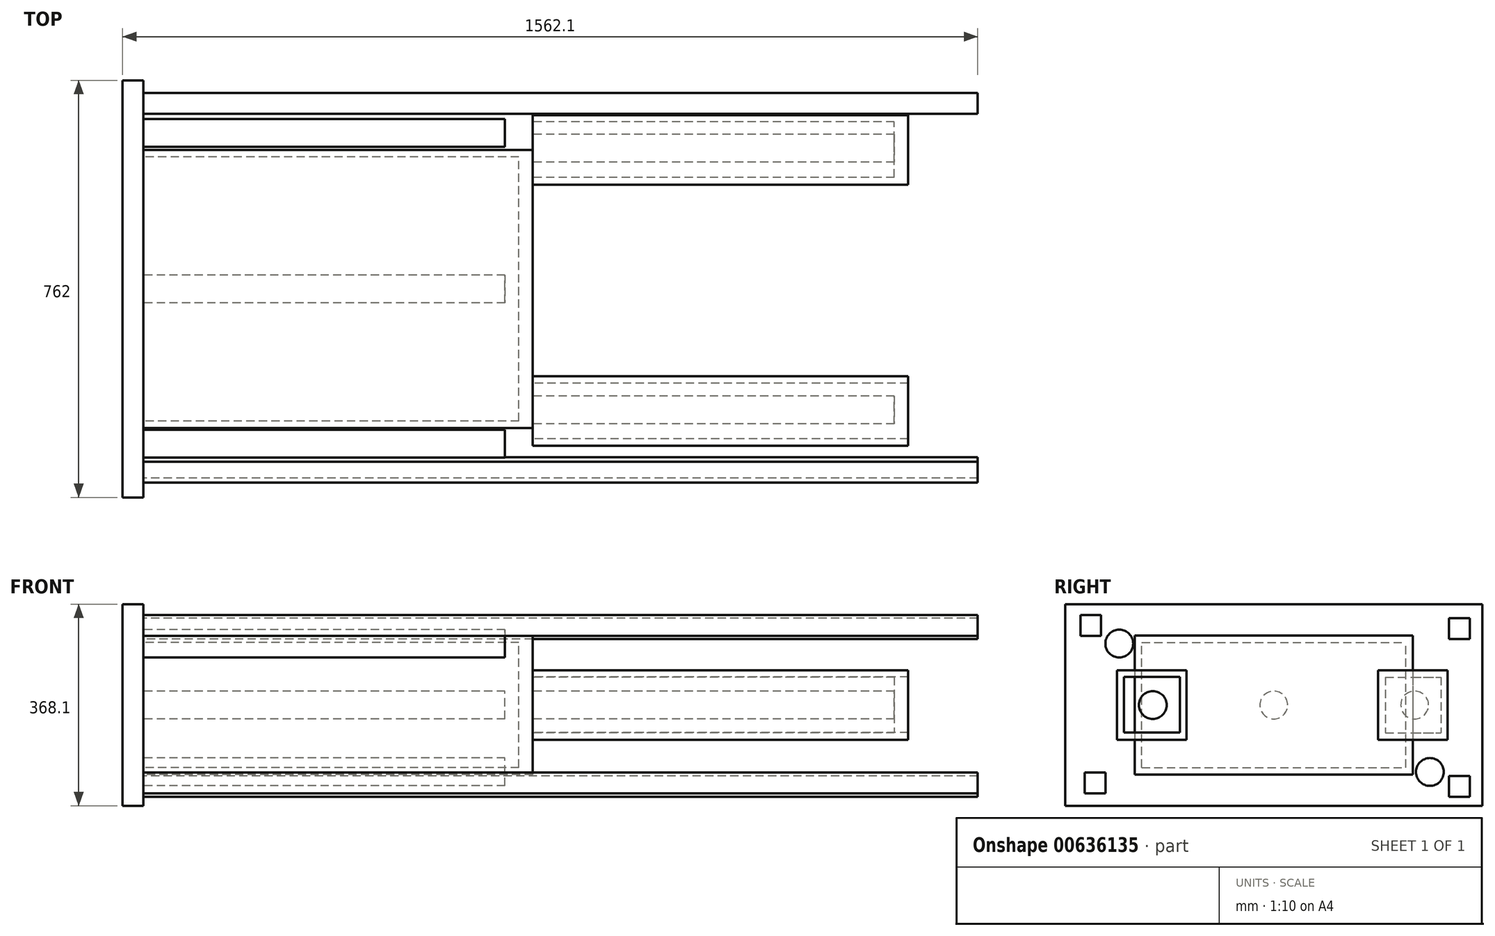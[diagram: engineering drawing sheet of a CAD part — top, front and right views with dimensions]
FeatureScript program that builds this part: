
annotation { "Feature Type Name" : "Feature", "Feature Type Description" : "" }
export const myFeature = defineFeature(function(context is Context, id is Id, definition is map)
    precondition{}
    {
        {
            var Q0;
            Q0=qCreatedBy(makeId("Right.planeOp"),FACE);
            var sketch = newSketch(context, id + "F0", { "sketchPlane" : qUnion([Q0])});
            skLineSegment(sketch, "E0.bottom", {"start": v(254, 127) * mm, "end": v(-254, 127) * mm});
            skLineSegment(sketch, "E0.top", {"start": v(254, -127) * mm, "end": v(-254, -127) * mm});
            skLineSegment(sketch, "E0.left", {"start": v(254, 127) * mm, "end": v(254, -127) * mm});
            skLineSegment(sketch, "E0.right", {"start": v(-254, 127) * mm, "end": v(-254, -127) * mm});
            skPoint(sketch, "E0.middle", {"position": v(0, 0) * mm});
            skSolve(sketch);
        }
        {
            var Q0;
            Q0 = qSketchRegion(id + "F0", true);
            extrude(context, id + "F1", {"entities" : qUnion([Q0]), "depth" : 711.2 * mm, "offsetDistance" : 25.4 * mm});
        }
        {
            var Q0;
            Q0=makeQuery(id+"F1.opExtrude","CAP_FACE",FACE,{"disambiguationData":[OSD([sQuery(id+"F0.wireOp",EDGE,"E0.bottom"),sQuery(id+"F0.wireOp",EDGE,"E0.top"),sQuery(id+"F0.wireOp",EDGE,"E0.left"),sQuery(id+"F0.wireOp",EDGE,"E0.right")])],"isStart":true});
            var sketch = newSketch(context, id + "F2", { "sketchPlane" : qUnion([Q0])});
            skLineSegment(sketch, "E1.bottom", {"start": v(241.3, -114.3) * mm, "end": v(-241.3, -114.3) * mm});
            skLineSegment(sketch, "E1.top", {"start": v(241.3, 114.3) * mm, "end": v(-241.3, 114.3) * mm});
            skLineSegment(sketch, "E1.left", {"start": v(241.3, -114.3) * mm, "end": v(241.3, 114.3) * mm});
            skLineSegment(sketch, "E1.right", {"start": v(-241.3, -114.3) * mm, "end": v(-241.3, 114.3) * mm});
            skPoint(sketch, "E1.middle", {"position": v(0, 0) * mm});
            skSolve(sketch);
        }
        {
            var Q0;
            Q0=makeQuery(id+"F2.imprint","IMPRINT",FACE,{"disambiguationData":[TD([[makeQuery(id+"F2.imprint","IMPRINT",EDGE,{"derivedFrom":sQuery(id+"F2.wireOp",EDGE,"E1.bottom")}),-1.0]])]});
            extrude(context, id + "F3", {"entities" : qUnion([Q0]), "operationType" : NewBodyOperationType.REMOVE, "oppositeDirection" : true, "depth" : 685.8 * mm, "offsetDistance" : 25.4 * mm});
        }
        {
            var Q0;
            Q0=qCreatedBy(makeId("Right.planeOp"),FACE);
            var sketch = newSketch(context, id + "F4", { "sketchPlane" : qUnion([Q0])});
            skCircle(sketch, "E2", {"center": v(0, 0) * mm, "radius": 25.4 * mm});
            skSolve(sketch);
        }
        {
            var Q0;
            Q0=makeQuery(id+"F4.imprint","IMPRINT",FACE,{"disambiguationData":[TD([[makeQuery(id+"F4.imprint","IMPRINT",EDGE,{"derivedFrom":sQuery(id+"F4.wireOp",EDGE,"E2")}),1.0]])]});
            extrude(context, id + "F5", {"entities" : qUnion([Q0]), "depth" : 660.4 * mm, "offsetDistance" : 25.4 * mm});
        }
        {
            var Q0;
            Q0=makeQuery(id+"F1.opExtrude","CAP_FACE",FACE,{"disambiguationData":[OSD([sQuery(id+"F0.wireOp",EDGE,"E0.bottom"),sQuery(id+"F0.wireOp",EDGE,"E0.top"),sQuery(id+"F0.wireOp",EDGE,"E0.left"),sQuery(id+"F0.wireOp",EDGE,"E0.right")])],"isStart":false});
            var sketch = newSketch(context, id + "F6", { "sketchPlane" : qUnion([Q0])});
            skLineSegment(sketch, "E3.bottom", {"start": v(-286.75, 63.5) * mm, "end": v(-159.75, 63.5) * mm});
            skLineSegment(sketch, "E3.top", {"start": v(-286.75, -63.5) * mm, "end": v(-159.75, -63.5) * mm});
            skLineSegment(sketch, "E3.left", {"start": v(-286.75, 63.5) * mm, "end": v(-286.75, -63.5) * mm});
            skLineSegment(sketch, "E3.right", {"start": v(-159.75, 63.5) * mm, "end": v(-159.75, -63.5) * mm});
            skPoint(sketch, "E3.middle", {"position": v(-223.25, 0) * mm});
            skSolve(sketch);
        }
        {
            var Q0;
            Q0=makeQuery(id+"F6.imprint","IMPRINT",FACE,{"disambiguationData":[TD([[makeQuery(id+"F6.imprint","IMPRINT",EDGE,{"derivedFrom":sQuery(id+"F6.wireOp",EDGE,"E3.bottom")}),-1.0]])]});
            extrude(context, id + "F7", {"entities" : qUnion([Q0]), "operationType" : NewBodyOperationType.ADD, "depth" : 685.8 * mm, "offsetDistance" : 25.4 * mm});
        }
        {
            var Q0;
            Q0=makeQuery(id+"F1.opExtrude","CAP_FACE",FACE,{"disambiguationData":[OSD([sQuery(id+"F0.wireOp",EDGE,"E0.bottom"),sQuery(id+"F0.wireOp",EDGE,"E0.top"),sQuery(id+"F0.wireOp",EDGE,"E0.left"),sQuery(id+"F0.wireOp",EDGE,"E0.right")])],"isStart":false});
            var sketch = newSketch(context, id + "F8", { "sketchPlane" : qUnion([Q0])});
            skLineSegment(sketch, "E4.bottom", {"start": v(-171.9, -50.19) * mm, "end": v(-273.5, -50.19) * mm});
            skLineSegment(sketch, "E4.top", {"start": v(-171.9, 51.41) * mm, "end": v(-273.5, 51.41) * mm});
            skLineSegment(sketch, "E4.left", {"start": v(-171.9, -50.19) * mm, "end": v(-171.9, 51.41) * mm});
            skLineSegment(sketch, "E4.right", {"start": v(-273.5, -50.19) * mm, "end": v(-273.5, 51.41) * mm});
            skSolve(sketch);
        }
        {
            var Q0;
            Q0=makeQuery(id+"F8.imprint","IMPRINT",FACE,{"disambiguationData":[TD([[makeQuery(id+"F8.imprint","IMPRINT",EDGE,{"derivedFrom":sQuery(id+"F8.wireOp",EDGE,"E4.bottom")}),-1.0]])]});
            extrude(context, id + "F9", {"entities" : qUnion([Q0]), "operationType" : NewBodyOperationType.REMOVE, "depth" : 685.8 * mm, "offsetDistance" : 25.4 * mm});
        }
        {
            var Q0;
            Q0=makeQuery(id+"F1.opExtrude","CAP_FACE",FACE,{"disambiguationData":[OSD([sQuery(id+"F0.wireOp",EDGE,"E0.bottom"),sQuery(id+"F0.wireOp",EDGE,"E0.top"),sQuery(id+"F0.wireOp",EDGE,"E0.left"),sQuery(id+"F0.wireOp",EDGE,"E0.right")])],"isStart":false});
            var sketch = newSketch(context, id + "F10", { "sketchPlane" : qUnion([Q0])});
            skCircle(sketch, "E5", {"center": v(-221.22, 0) * mm, "radius": 25.4 * mm});
            skSolve(sketch);
        }
        {
            var Q0;
            Q0=makeQuery(id+"F10.imprint","IMPRINT",FACE,{"disambiguationData":[TD([[makeQuery(id+"F10.imprint","IMPRINT",EDGE,{"derivedFrom":sQuery(id+"F10.wireOp",EDGE,"E5")}),1.0]])]});
            extrude(context, id + "F11", {"entities" : qUnion([Q0]), "operationType" : NewBodyOperationType.ADD, "depth" : 660.4 * mm, "offsetDistance" : 25.4 * mm});
        }
        {
            var Q0;
            Q0=qCreatedBy(makeId("Right.planeOp"),FACE);
            var sketch = newSketch(context, id + "F12", { "sketchPlane" : qUnion([Q0])});
            skLineSegment(sketch, "E6.bottom", {"start": v(-381, 184.05) * mm, "end": v(381, 184.05) * mm});
            skLineSegment(sketch, "E6.top", {"start": v(-381, -184.05) * mm, "end": v(381, -184.05) * mm});
            skLineSegment(sketch, "E6.left", {"start": v(-381, 184.05) * mm, "end": v(-381, -184.05) * mm});
            skLineSegment(sketch, "E6.right", {"start": v(381, 184.05) * mm, "end": v(381, -184.05) * mm});
            skPoint(sketch, "E6.middle", {"position": v(0, 0) * mm});
            skSolve(sketch);
        }
        {
            var Q0;
            Q0=makeQuery(id+"F12.imprint","IMPRINT",FACE,{"disambiguationData":[TD([[makeQuery(id+"F12.imprint","IMPRINT",EDGE,{"derivedFrom":sQuery(id+"F12.wireOp",EDGE,"E6.bottom")}),-1.0]])]});
            extrude(context, id + "F13", {"entities" : qUnion([Q0]), "oppositeDirection" : true, "depth" : 38.1 * mm, "offsetDistance" : 25.4 * mm});
        }
        {
            var Q0;
            Q0=makeQuery(id+"F1.opExtrude","CAP_FACE",FACE,{"disambiguationData":[OSD([sQuery(id+"F0.wireOp",EDGE,"E0.bottom"),sQuery(id+"F0.wireOp",EDGE,"E0.top"),sQuery(id+"F0.wireOp",EDGE,"E0.left"),sQuery(id+"F0.wireOp",EDGE,"E0.right")])],"isStart":false});
            var sketch = newSketch(context, id + "F14", { "sketchPlane" : qUnion([Q0])});
            skLineSegment(sketch, "E7.bottom", {"start": v(317.5, 63.5) * mm, "end": v(190.5, 63.5) * mm});
            skLineSegment(sketch, "E7.top", {"start": v(317.5, -63.5) * mm, "end": v(190.5, -63.5) * mm});
            skLineSegment(sketch, "E7.left", {"start": v(317.5, 63.5) * mm, "end": v(317.5, -63.5) * mm});
            skLineSegment(sketch, "E7.right", {"start": v(190.5, 63.5) * mm, "end": v(190.5, -63.5) * mm});
            skPoint(sketch, "E7.middle", {"position": v(254, 0) * mm});
            skSolve(sketch);
        }
        {
            var Q0;
            {var subQ0=sQuery(id+"F14.wireOp",EDGE,"E7.right");Q0=makeQuery(id+"F14.imprint","IMPRINT",FACE,{"disambiguationData":[TD([[makeQuery(id+"F14.imprint","IMPRINT",EDGE,{"derivedFrom":subQ0}),1.0]])]});}
            var Q1;
            {var subQ0=sQuery(id+"F14.wireOp",EDGE,"E7.left");Q1=makeQuery(id+"F14.imprint","IMPRINT",FACE,{"disambiguationData":[TD([[makeQuery(id+"F14.imprint","IMPRINT",EDGE,{"derivedFrom":subQ0}),-1.0]])]});}
            extrude(context, id + "F15", {"entities" : qUnion([Q0, Q1]), "operationType" : NewBodyOperationType.ADD, "depth" : 685.8 * mm, "offsetDistance" : 25.4 * mm});
        }
        {
            var Q0;
            Q0=makeQuery(id+"F1.opExtrude","CAP_FACE",FACE,{"disambiguationData":[OSD([sQuery(id+"F0.wireOp",EDGE,"E0.bottom"),sQuery(id+"F0.wireOp",EDGE,"E0.top"),sQuery(id+"F0.wireOp",EDGE,"E0.left"),sQuery(id+"F0.wireOp",EDGE,"E0.right")])],"isStart":false});
            var sketch = newSketch(context, id + "F16", { "sketchPlane" : qUnion([Q0])});
            skLineSegment(sketch, "E8.bottom", {"start": v(203.8, 50.8) * mm, "end": v(305.4, 50.8) * mm});
            skLineSegment(sketch, "E8.top", {"start": v(203.8, -50.8) * mm, "end": v(305.4, -50.8) * mm});
            skLineSegment(sketch, "E8.left", {"start": v(203.8, 50.8) * mm, "end": v(203.8, -50.8) * mm});
            skLineSegment(sketch, "E8.right", {"start": v(305.4, 50.8) * mm, "end": v(305.4, -50.8) * mm});
            skPoint(sketch, "E8.middle", {"position": v(254.6, 0) * mm});
            skSolve(sketch);
        }
        {
            var Q0;
            Q0=makeQuery(id+"F16.imprint","IMPRINT",FACE,{"disambiguationData":[TD([[makeQuery(id+"F16.imprint","IMPRINT",EDGE,{"derivedFrom":sQuery(id+"F16.wireOp",EDGE,"E8.bottom")}),-1.0]])]});
            extrude(context, id + "F17", {"entities" : qUnion([Q0]), "operationType" : NewBodyOperationType.REMOVE, "depth" : 660.4 * mm, "offsetDistance" : 25.4 * mm});
        }
        {
            var Q0;
            Q0=makeQuery(id+"F1.opExtrude","CAP_FACE",FACE,{"disambiguationData":[OSD([sQuery(id+"F0.wireOp",EDGE,"E0.bottom"),sQuery(id+"F0.wireOp",EDGE,"E0.top"),sQuery(id+"F0.wireOp",EDGE,"E0.left"),sQuery(id+"F0.wireOp",EDGE,"E0.right")])],"isStart":false});
            var sketch = newSketch(context, id + "F18", { "sketchPlane" : qUnion([Q0])});
            skCircle(sketch, "E9", {"center": v(257.24, 0) * mm, "radius": 25.4 * mm});
            skSolve(sketch);
        }
        {
            var Q0;
            Q0=makeQuery(id+"F18.imprint","IMPRINT",FACE,{"disambiguationData":[TD([[makeQuery(id+"F18.imprint","IMPRINT",EDGE,{"derivedFrom":sQuery(id+"F18.wireOp",EDGE,"E9")}),1.0]])]});
            extrude(context, id + "F19", {"entities" : qUnion([Q0]), "depth" : 660.4 * mm, "offsetDistance" : 25.4 * mm});
        }
        {
            var Q0;
            Q0=makeQuery(id+"F13.opExtrude","CAP_FACE",FACE,{"disambiguationData":[OSD([sQuery(id+"F12.wireOp",EDGE,"E6.bottom"),sQuery(id+"F12.wireOp",EDGE,"E6.top"),sQuery(id+"F12.wireOp",EDGE,"E6.left"),sQuery(id+"F12.wireOp",EDGE,"E6.right")])],"isStart":true});
            var sketch = newSketch(context, id + "F20", { "sketchPlane" : qUnion([Q0])});
            skLineSegment(sketch, "E10.bottom", {"start": v(-353.51, 164.15) * mm, "end": v(-315.41, 164.15) * mm});
            skLineSegment(sketch, "E10.top", {"start": v(-353.51, 126.05) * mm, "end": v(-315.41, 126.05) * mm});
            skLineSegment(sketch, "E10.left", {"start": v(-353.51, 164.15) * mm, "end": v(-353.51, 126.05) * mm});
            skLineSegment(sketch, "E10.right", {"start": v(-315.41, 164.15) * mm, "end": v(-315.41, 126.05) * mm});
            skPoint(sketch, "E10.middle", {"position": v(-334.46, 145.1) * mm});
            skLineSegment(sketch, "E11.bottom", {"start": v(-307.52, -123.32) * mm, "end": v(-345.62, -123.32) * mm});
            skLineSegment(sketch, "E11.top", {"start": v(-307.52, -161.42) * mm, "end": v(-345.62, -161.42) * mm});
            skLineSegment(sketch, "E11.left", {"start": v(-307.52, -123.32) * mm, "end": v(-307.52, -161.42) * mm});
            skLineSegment(sketch, "E11.right", {"start": v(-345.62, -123.32) * mm, "end": v(-345.62, -161.42) * mm});
            skPoint(sketch, "E11.middle", {"position": v(-326.57, -142.37) * mm});
            skLineSegment(sketch, "E12.bottom", {"start": v(357.93, 158.52) * mm, "end": v(319.83, 158.52) * mm});
            skLineSegment(sketch, "E12.top", {"start": v(357.93, 120.42) * mm, "end": v(319.83, 120.42) * mm});
            skLineSegment(sketch, "E12.left", {"start": v(357.93, 158.52) * mm, "end": v(357.93, 120.42) * mm});
            skLineSegment(sketch, "E12.right", {"start": v(319.83, 158.52) * mm, "end": v(319.83, 120.42) * mm});
            skPoint(sketch, "E12.middle", {"position": v(338.88, 139.47) * mm});
            skLineSegment(sketch, "E13.bottom", {"start": v(320.2, -129.37) * mm, "end": v(358.3, -129.37) * mm});
            skLineSegment(sketch, "E13.top", {"start": v(320.2, -167.47) * mm, "end": v(358.3, -167.47) * mm});
            skLineSegment(sketch, "E13.left", {"start": v(320.2, -129.37) * mm, "end": v(320.2, -167.47) * mm});
            skLineSegment(sketch, "E13.right", {"start": v(358.3, -129.37) * mm, "end": v(358.3, -167.47) * mm});
            skPoint(sketch, "E13.middle", {"position": v(339.24, -148.42) * mm});
            skSolve(sketch);
        }
        {
            var Q0;
            Q0=makeQuery(id+"F20.imprint","IMPRINT",FACE,{"disambiguationData":[TD([[makeQuery(id+"F20.imprint","IMPRINT",EDGE,{"derivedFrom":sQuery(id+"F20.wireOp",EDGE,"E13.bottom")}),-1.0]])]});
            var Q1;
            Q1=makeQuery(id+"F20.imprint","IMPRINT",FACE,{"disambiguationData":[TD([[makeQuery(id+"F20.imprint","IMPRINT",EDGE,{"derivedFrom":sQuery(id+"F20.wireOp",EDGE,"E12.bottom")}),1.0]])]});
            var Q2;
            Q2=makeQuery(id+"F20.imprint","IMPRINT",FACE,{"disambiguationData":[TD([[makeQuery(id+"F20.imprint","IMPRINT",EDGE,{"derivedFrom":sQuery(id+"F20.wireOp",EDGE,"E10.bottom")}),-1.0]])]});
            var Q3;
            Q3=makeQuery(id+"F20.imprint","IMPRINT",FACE,{"disambiguationData":[TD([[makeQuery(id+"F20.imprint","IMPRINT",EDGE,{"derivedFrom":sQuery(id+"F20.wireOp",EDGE,"E11.bottom")}),1.0]])]});
            extrude(context, id + "F21", {"entities" : qUnion([Q0, Q1, Q2, Q3]), "operationType" : NewBodyOperationType.ADD, "depth" : 1524 * mm, "offsetDistance" : 25.4 * mm});
        }
        {
            var Q0;
            Q0=makeQuery(id+"F13.opExtrude","CAP_FACE",FACE,{"disambiguationData":[OSD([sQuery(id+"F12.wireOp",EDGE,"E6.bottom"),sQuery(id+"F12.wireOp",EDGE,"E6.top"),sQuery(id+"F12.wireOp",EDGE,"E6.left"),sQuery(id+"F12.wireOp",EDGE,"E6.right")])],"isStart":true});
            var sketch = newSketch(context, id + "F22", { "sketchPlane" : qUnion([Q0])});
            skCircle(sketch, "E14", {"center": v(-282.36, 112.1) * mm, "radius": 25.4 * mm});
            skCircle(sketch, "E15", {"center": v(285.15, -122.34) * mm, "radius": 25.4 * mm});
            skSolve(sketch);
        }
        {
            var Q0;
            Q0=makeQuery(id+"F22.imprint","IMPRINT",FACE,{"disambiguationData":[TD([[makeQuery(id+"F22.imprint","IMPRINT",EDGE,{"derivedFrom":sQuery(id+"F22.wireOp",EDGE,"E14")}),1.0]])]});
            var Q1;
            Q1=makeQuery(id+"F22.imprint","IMPRINT",FACE,{"disambiguationData":[TD([[makeQuery(id+"F22.imprint","IMPRINT",EDGE,{"derivedFrom":sQuery(id+"F22.wireOp",EDGE,"E15")}),1.0]])]});
            extrude(context, id + "F23", {"entities" : qUnion([Q0, Q1]), "depth" : 660.4 * mm, "offsetDistance" : 25.4 * mm});
        }
    });
